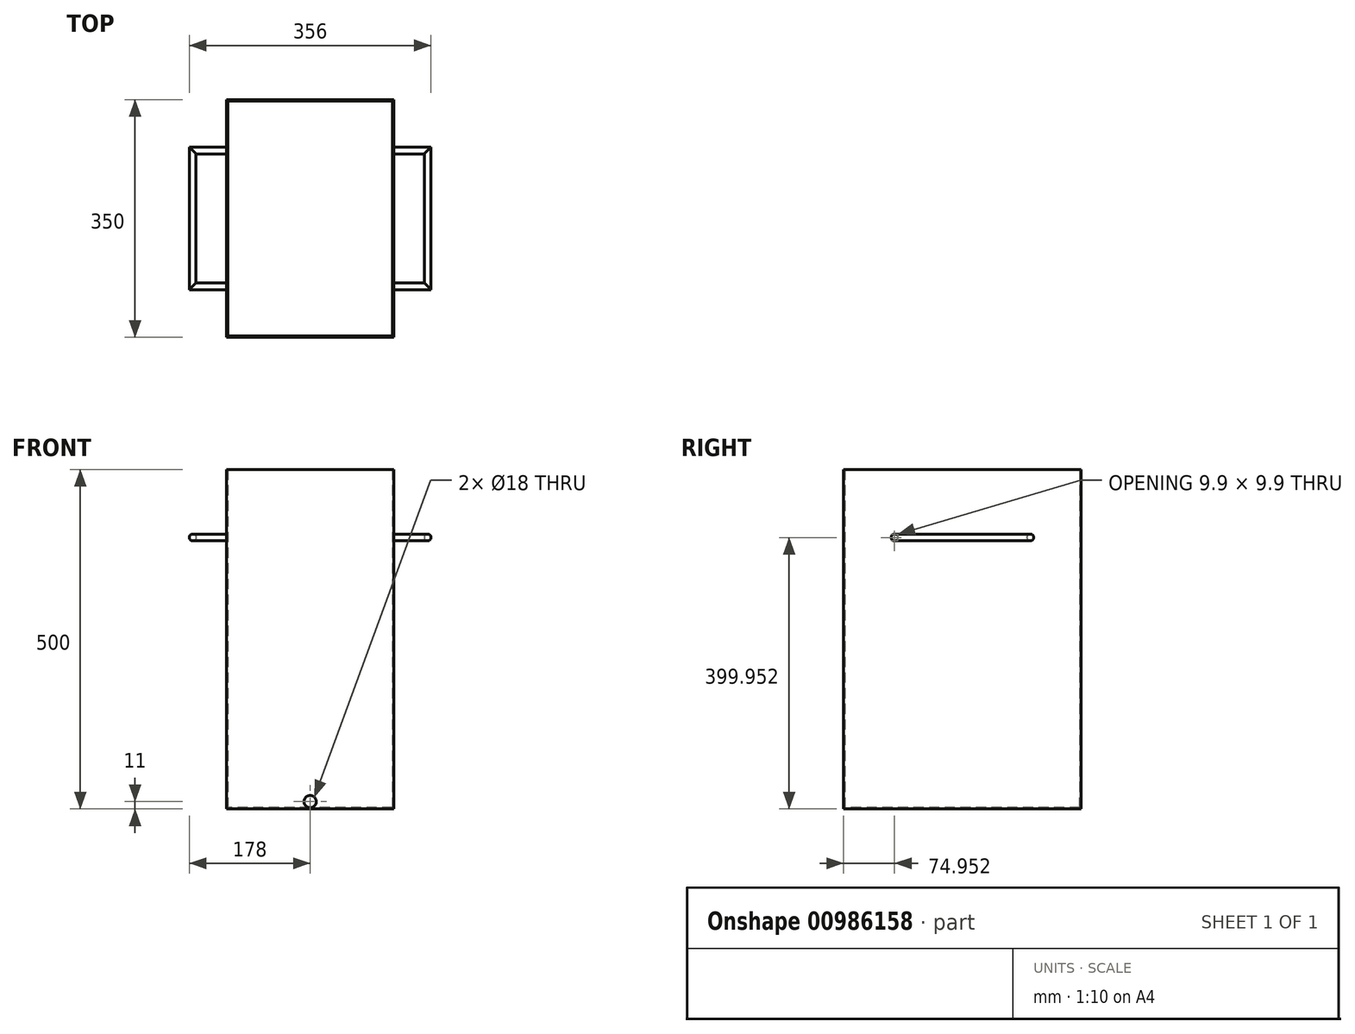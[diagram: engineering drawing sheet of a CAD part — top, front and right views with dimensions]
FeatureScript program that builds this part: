
annotation { "Feature Type Name" : "Feature", "Feature Type Description" : "" }
export const myFeature = defineFeature(function(context is Context, id is Id, definition is map)
    precondition{}
    {
        {
            var Q0;
            Q0=qCreatedBy(makeId("Right.planeOp"),FACE);
            var sketch = newSketch(context, id + "F0", { "sketchPlane" : qUnion([Q0])});
            skLineSegment(sketch, "E0", {"start": v(175, 0) * mm, "end": v(175, -500) * mm});
            skLineSegment(sketch, "E1", {"start": v(175, -500) * mm, "end": v(-175, -500) * mm});
            skLineSegment(sketch, "E2", {"start": v(173, 0) * mm, "end": v(175, 0) * mm});
            skLineSegment(sketch, "E3", {"start": v(-173, 0) * mm, "end": v(-175, 0) * mm});
            skLineSegment(sketch, "E4", {"start": v(-175, 0) * mm, "end": v(-175, -500) * mm});
            skLineSegment(sketch, "E5", {"start": v(-173, 0) * mm, "end": v(-173, -498) * mm});
            skLineSegment(sketch, "E6", {"start": v(173, 0) * mm, "end": v(173, -498) * mm});
            skLineSegment(sketch, "E7", {"start": v(173, -498) * mm, "end": v(-173, -498) * mm});
            skSolve(sketch);
        }
        {
            var Q0;
            Q0=makeQuery(id+"F0.imprint","IMPRINT",FACE,{"disambiguationData":[TD([[makeQuery(id+"F0.imprint","IMPRINT",EDGE,{"derivedFrom":sQuery(id+"F0.wireOp",EDGE,"Chy8j9AN-zMDN-jnD6-xvX6-RCg8pUgCE5Ah")}),-1.0]])]});
            var Q1;
            Q1=makeQuery(id+"F0.imprint","IMPRINT",FACE,{"disambiguationData":[TD([[makeQuery(id+"F0.imprint","IMPRINT",EDGE,{"derivedFrom":sQuery(id+"F0.wireOp",EDGE,"bfxHKpT6-eyvY-QHHH-y0TI-8smu4qWN1G2s")}),1.0]])]});
            var Q2;
            Q2=makeQuery(id+"F0.imprint","IMPRINT",FACE,{"disambiguationData":[TD([[makeQuery(id+"F0.imprint","IMPRINT",EDGE,{"derivedFrom":sQuery(id+"F0.wireOp",EDGE,"E0")}),-1.0]])]});
            extrude(context, id + "F1", {"entities" : qUnion([Q0, Q1, Q2]), "depth" : 123 * mm, "offsetDistance" : 25 * mm});
        }
        {
            var Q0;
            Q0=makeQuery(id+"F1.opExtrude","CAP_FACE",FACE,{"disambiguationData":[OSD([sQuery(id+"F0.wireOp",EDGE,"Chy8j9AN-zMDN-jnD6-xvX6-RCg8pUgCE5Ah"),sQuery(id+"F0.wireOp",EDGE,"E0"),sQuery(id+"F0.wireOp",EDGE,"ud0wCLYM-TfRJ-dMwY-h2ru-oExgMNDcEtCX"),sQuery(id+"F0.wireOp",EDGE,"G5wE1AY4-myaK-8NTK-Es47-a17ob7Y6Co6d"),sQuery(id+"F0.wireOp",EDGE,"nKNq8AH6-1NsQ-kvFP-YseY-KZsH4UJA0EIO"),sQuery(id+"F0.wireOp",EDGE,"672f01d3-ed75-436a-ba79-6e114271b8810.MirrorCS"),sQuery(id+"F0.wireOp",EDGE,"57a6388c-164a-4118-8ff6-5751f3e2cf150.MirrorCS"),sQuery(id+"F0.wireOp",EDGE,"298c5bd2-e8ee-4727-9836-d7d8b11258820.MirrorCS"),sQuery(id+"F0.wireOp",EDGE,"1c2af689-9e01-4c68-aa1b-bd6baa432c200.MirrorCS"),sQuery(id+"F0.wireOp",EDGE,"ee5c5fc5-6be6-4005-9d72-73e9a0f6ed7b0.MirrorCS")])],"isStart":false});
            cPlane(context, id + "F2", {"entities" : qUnion([Q0]), "cplaneType" : CPlaneType.OFFSET, "offset" : 0 * mm, "width" : 150 * mm, "height" : 150 * mm});
        }
        {
            var Q0;
            Q0=qCreatedBy(id+"F2.planeOp",FACE);
            var sketch = newSketch(context, id + "F3", { "sketchPlane" : qUnion([Q0])});
            skLineSegment(sketch, "E8", {"start": v(0, 0) * mm, "end": v(175, 0) * mm});
            skLineSegment(sketch, "E9", {"start": v(175, 0) * mm, "end": v(175, -500) * mm});
            skLineSegment(sketch, "E10", {"start": v(175, -500) * mm, "end": v(-175, -500) * mm});
            skLineSegment(sketch, "E11", {"start": v(-175, -500) * mm, "end": v(-175, 0) * mm});
            skLineSegment(sketch, "E12", {"start": v(-175, 0) * mm, "end": v(0, 0) * mm});
            skSolve(sketch);
        }
        {
            var Q0;
            Q0=makeQuery(id+"F3.imprint","IMPRINT",FACE,{"disambiguationData":[TD([[makeQuery(id+"F3.imprint","IMPRINT",EDGE,{"derivedFrom":sQuery(id+"F3.wireOp",EDGE,"E8")}),-1.0]])]});
            extrude(context, id + "F4", {"entities" : qUnion([Q0]), "operationType" : NewBodyOperationType.ADD, "oppositeDirection" : true, "depth" : 2 * mm, "offsetDistance" : 25 * mm});
        }
        {
            var Q0;
            Q0=qCreatedBy(id+"F2.planeOp",FACE);
            var sketch = newSketch(context, id + "F5", { "sketchPlane" : qUnion([Q0])});
            skLineSegment(sketch, "E13", {"start": v(0, 0) * mm, "end": v(0, -100) * mm});
            skLineSegment(sketch, "E14", {"start": v(0, -100) * mm, "end": v(100, -100) * mm});
            skCircle(sketch, "E15", {"center": v(100, -100) * mm, "radius": 5 * mm});
            skSolve(sketch);
        }
        {
            var Q0;
            Q0=makeQuery(id+"F4.boolean.opBoolean","MERGE",FACE,{"derivedFrom":[makeQuery(id+"F1.opExtrude","SWEPT_FACE",FACE,{"disambiguationData":[OSD([sQuery(id+"F0.wireOp",EDGE,"E2")])]}),makeQuery(id+"F1.opExtrude","SWEPT_FACE",FACE,{"disambiguationData":[OSD([sQuery(id+"F0.wireOp",EDGE,"E3")])]}),makeQuery(id+"F4.opExtrude","SWEPT_FACE",FACE,{"disambiguationData":[OSD([sQuery(id+"F3.wireOp",EDGE,"E8"),sQuery(id+"F3.wireOp",EDGE,"E12")])]})]});
            cPlane(context, id + "F6", {"entities" : qUnion([Q0]), "cplaneType" : CPlaneType.OFFSET, "offset" : 100 * mm, "oppositeDirection" : true, "width" : 150 * mm, "height" : 150 * mm});
        }
        {
            var Q0;
            Q0=qCreatedBy(id+"F6.planeOp",FACE);
            var sketch = newSketch(context, id + "F7", { "sketchPlane" : qUnion([Q0])});
            skLineSegment(sketch, "E16", {"start": v(123, 100) * mm, "end": v(173, 100) * mm});
            skLineSegment(sketch, "E17", {"start": v(173, 100) * mm, "end": v(173, -100) * mm});
            skLineSegment(sketch, "E18", {"start": v(173, -100) * mm, "end": v(123, -100) * mm});
            skSolve(sketch);
        }
        {
            var Q0;
            Q0=makeQuery(id+"F5.imprint","IMPRINT",FACE,{"disambiguationData":[TD([[makeQuery(id+"F5.imprint","IMPRINT",EDGE,{"derivedFrom":sQuery(id+"F5.wireOp",EDGE,"E15")}),1.0]])]});
            var Q1;
            Q1=sQuery(id+"F7.wireOp",EDGE,"E16");
            var Q2;
            Q2=sQuery(id+"F7.wireOp",EDGE,"E17");
            var Q3;
            Q3=sQuery(id+"F7.wireOp",EDGE,"E18");
            sweep(context, id + "F8", {"profiles" : qUnion([Q0]), "path" : qUnion([Q1, Q2, Q3])});
        }
        {
            var Q0;
            Q0=makeQuery(id+"F1.opExtrude","SWEPT_BODY",BODY,{"disambiguationData":[OSD([sQuery(id+"F0.wireOp",EDGE,"E0"),sQuery(id+"F0.wireOp",EDGE,"E1"),sQuery(id+"F0.wireOp",EDGE,"E2"),sQuery(id+"F0.wireOp",EDGE,"E3"),sQuery(id+"F0.wireOp",EDGE,"E4"),sQuery(id+"F0.wireOp",EDGE,"E5"),sQuery(id+"F0.wireOp",EDGE,"E6"),sQuery(id+"F0.wireOp",EDGE,"E7")])]});
            var Q1;
            Q1=makeQuery(id+"F8.opSweep","SWEPT_BODY",BODY,{"disambiguationData":[OSD([sQuery(id+"F5.wireOp",EDGE,"E15"),sQuery(id+"F7.wireOp",EDGE,"E18")])]});
            var Q2;
            Q2=makeQuery(id+"F1.opExtrude","CAP_FACE",FACE,{"disambiguationData":[OSD([sQuery(id+"F0.wireOp",EDGE,"E0"),sQuery(id+"F0.wireOp",EDGE,"E1"),sQuery(id+"F0.wireOp",EDGE,"E2"),sQuery(id+"F0.wireOp",EDGE,"E3"),sQuery(id+"F0.wireOp",EDGE,"E4"),sQuery(id+"F0.wireOp",EDGE,"E5"),sQuery(id+"F0.wireOp",EDGE,"E6"),sQuery(id+"F0.wireOp",EDGE,"E7")])],"isStart":true});
            mirror(context, id + "F9", {"operationType" : NewBodyOperationType.ADD, "entities" : qUnion([Q0, Q1]), "mirrorPlane" : qUnion([Q2])});
        }
        {
            var Q0;
            {var subQ0=makeQuery(id+"F1.opExtrude","SWEPT_FACE",FACE,{"disambiguationData":[OSD([sQuery(id+"F0.wireOp",EDGE,"E4")])]});Q0=makeQuery(id+"F9.boolean.opBoolean","MERGE",FACE,{"derivedFrom":[subQ0,makeQuery(id+"F9.opPattern","COPY",FACE,{"derivedFrom":subQ0,"instanceName":"1"})]});}
            cPlane(context, id + "F10", {"entities" : qUnion([Q0]), "cplaneType" : CPlaneType.OFFSET, "offset" : 0 * mm, "width" : 150 * mm, "height" : 150 * mm});
        }
        {
            var Q0;
            Q0=qCreatedBy(id+"F10.planeOp",FACE);
            var sketch = newSketch(context, id + "F11", { "sketchPlane" : qUnion([Q0])});
            skLineSegment(sketch, "E19", {"start": v(0, 0) * mm, "end": v(0, -489) * mm});
            skCircle(sketch, "E20", {"center": v(0, -489) * mm, "radius": 9 * mm});
            skSolve(sketch);
        }
        {
            var Q0;
            Q0=makeQuery(id+"F11.imprint","IMPRINT",FACE,{"disambiguationData":[TD([[makeQuery(id+"F11.imprint","IMPRINT",EDGE,{"derivedFrom":sQuery(id+"F11.wireOp",EDGE,"E20")}),1.0]])]});
            extrude(context, id + "F12", {"entities" : qUnion([Q0]), "operationType" : NewBodyOperationType.REMOVE, "oppositeDirection" : true, "depth" : 500 * mm, "offsetDistance" : 25 * mm});
        }
    });
